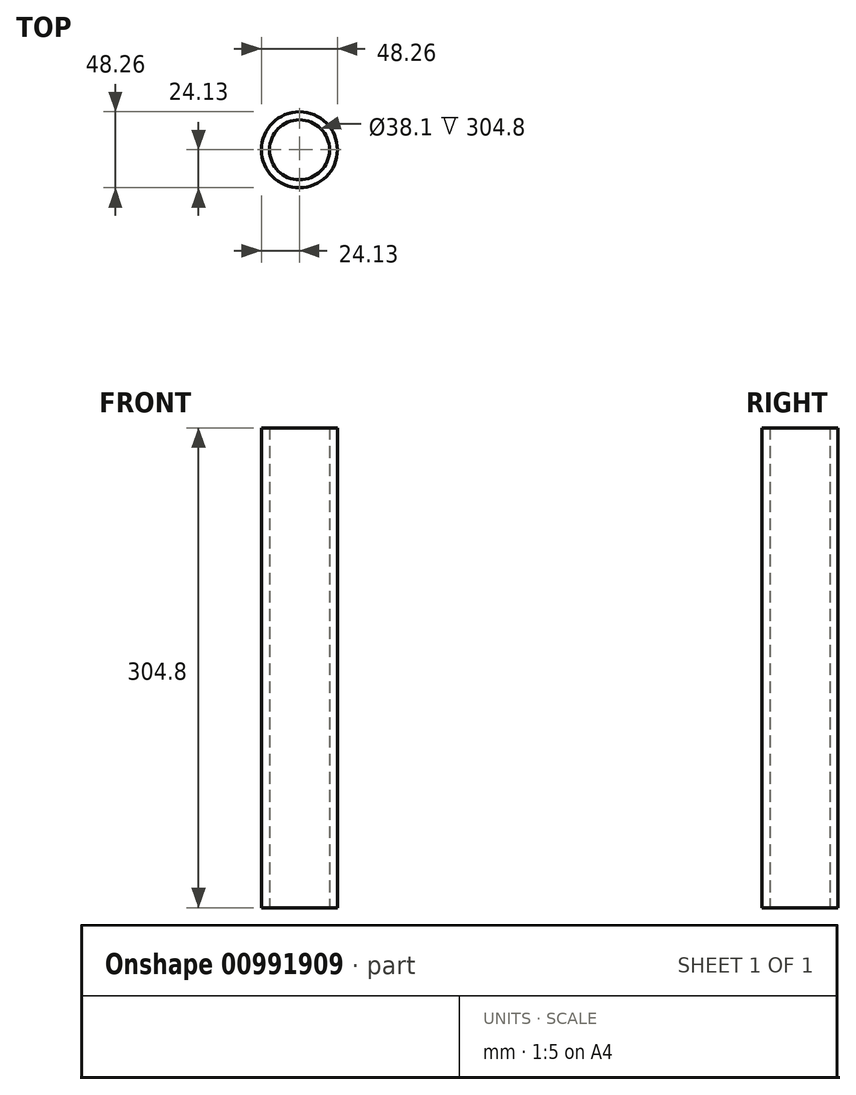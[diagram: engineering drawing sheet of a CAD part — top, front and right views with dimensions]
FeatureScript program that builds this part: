
annotation { "Feature Type Name" : "Feature", "Feature Type Description" : "" }
export const myFeature = defineFeature(function(context is Context, id is Id, definition is map)
    precondition{}
    {
        {
            var Q0;
            Q0=qCreatedBy(makeId("Top.planeOp"),FACE);
            var sketch = newSketch(context, id + "F0", { "sketchPlane" : qUnion([Q0])});
            skCircle(sketch, "E0", {"center": v(0, 0) * mm, "radius": 24.13 * mm});
            skCircle(sketch, "E1", {"center": v(0, 0) * mm, "radius": 19.05 * mm});
            skSolve(sketch);
        }
        {
            var Q0;
            Q0=makeQuery(id+"F0.imprint","IMPRINT",FACE,{"disambiguationData":[TD([[makeQuery(id+"F0.imprint","IMPRINT",EDGE,{"derivedFrom":sQuery(id+"F0.wireOp",EDGE,"E0")}),1.0]])]});
            extrude(context, id + "F1", {"entities" : qUnion([Q0]), "depth" : 304.8 * mm, "offsetDistance" : 25.4 * mm});
        }
    });
